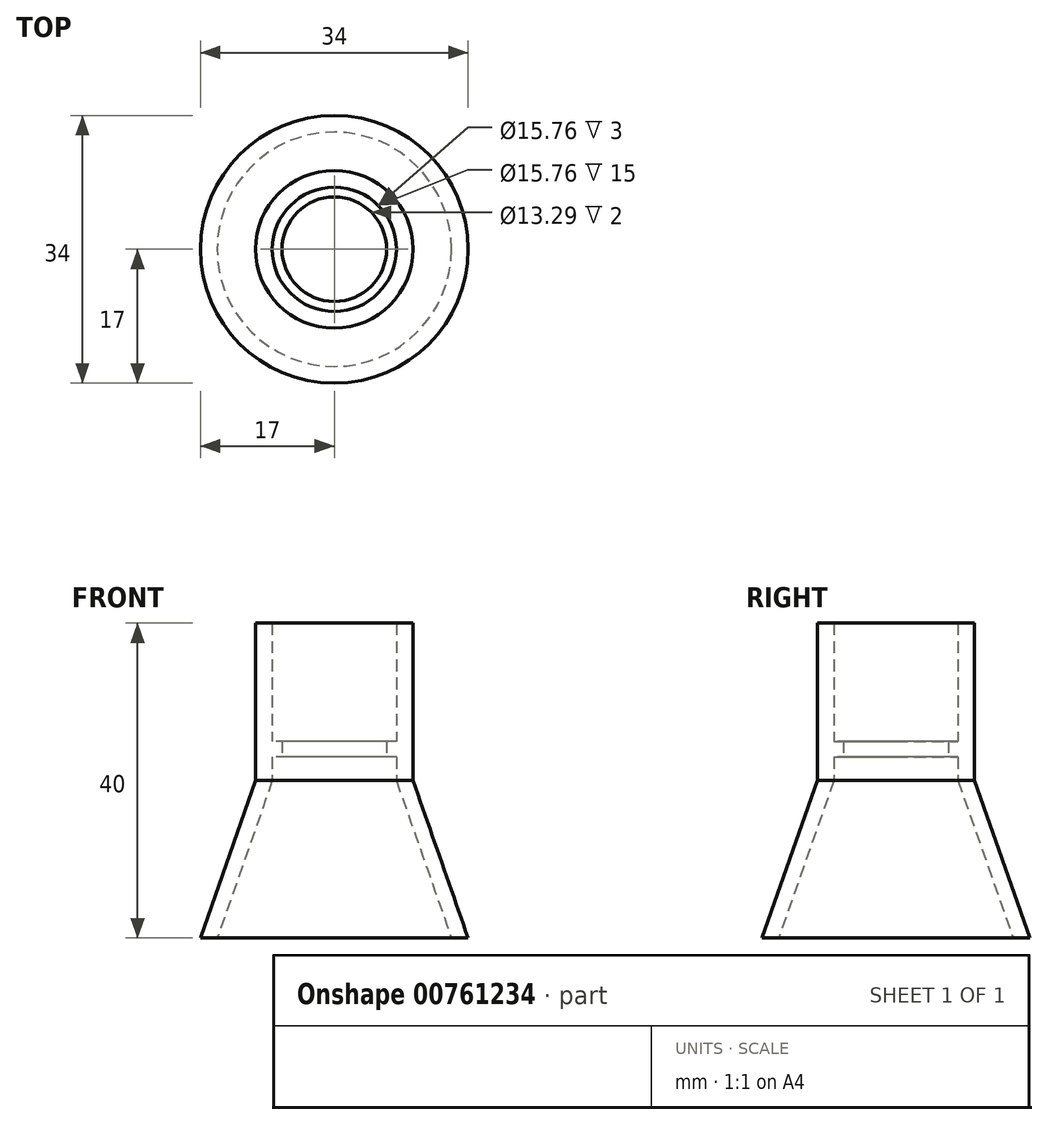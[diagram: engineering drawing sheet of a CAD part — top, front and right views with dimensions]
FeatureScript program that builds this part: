
annotation { "Feature Type Name" : "Feature", "Feature Type Description" : "" }
export const myFeature = defineFeature(function(context is Context, id is Id, definition is map)
    precondition{}
    {
        {
            var Q0;
            Q0=qCreatedBy(makeId("Top.planeOp"),FACE);
            cPlane(context, id + "F0", {"entities" : qUnion([Q0]), "cplaneType" : CPlaneType.OFFSET, "offset" : 20 * mm, "width" : 152.4 * mm, "height" : 152.4 * mm});
        }
        {
            var Q0;
            Q0=qCreatedBy(makeId("Top.planeOp"),FACE);
            var sketch = newSketch(context, id + "F1", { "sketchPlane" : qUnion([Q0])});
            skCircle(sketch, "E0", {"center": v(0, 0) * mm, "radius": 17 * mm});
            skSolve(sketch);
        }
        {
            var Q0;
            Q0=qCreatedBy(id+"F0.planeOp",FACE);
            var sketch = newSketch(context, id + "F2", { "sketchPlane" : qUnion([Q0])});
            skCircle(sketch, "E1", {"center": v(0, 0) * mm, "radius": 10 * mm});
            skSolve(sketch);
        }
        {
            var Q0;
            Q0=qSketchRegion(id+"F1",true);
            var Q1;
            Q1=qSketchRegion(id+"F2",true);
            loft(context, id + "F3", {"sheetProfilesArray" : [{ "sheetProfileEntities" : qUnion([Q0]) }, { "sheetProfileEntities" : qUnion([Q1]) }]});
        }
        {
            var Q0;
            Q0=makeQuery(id+"F3.opLoft","CAP_FACE",FACE,{"disambiguationData":[OSD([makeQuery(id+"F2.imprint","IMPRINT",FACE,{"disambiguationData":[TD([[makeQuery(id+"F2.imprint","IMPRINT",EDGE,{"derivedFrom":sQuery(id+"F2.wireOp",EDGE,"E1")}),1.0]])]})])],"isStart":true});
            var Q1;
            Q1=makeQuery(id+"F3.opLoft","CAP_FACE",FACE,{"disambiguationData":[OSD([makeQuery(id+"F1.imprint","IMPRINT",FACE,{"disambiguationData":[TD([[makeQuery(id+"F1.imprint","IMPRINT",EDGE,{"derivedFrom":sQuery(id+"F1.wireOp",EDGE,"E0")}),1.0]])]})])],"isStart":true});
            shell(context, id + "F4", {"entities" : qUnion([Q0, Q1]), "thickness" : 2 * mm});
        }
        {
            var Q0;
            Q0=qCreatedBy(makeId("Top.planeOp"),FACE);
            cPlane(context, id + "F5", {"entities" : qUnion([Q0]), "cplaneType" : CPlaneType.OFFSET, "offset" : 23 * mm, "width" : 150 * mm, "height" : 150 * mm});
        }
        {
            var Q0;
            Q0=qCreatedBy(id+"F5.planeOp",FACE);
            var sketch = newSketch(context, id + "F6", { "sketchPlane" : qUnion([Q0])});
            skCircle(sketch, "E2", {"center": v(0, 0) * mm, "radius": 6.64 * mm});
            skCircle(sketch, "E3", {"center": v(0, 0) * mm, "radius": 9.64 * mm});
            skSolve(sketch);
        }
        {
            var Q0;
            Q0 = qSketchRegion(id + "F6", true);
            extrude(context, id + "F7", {"entities" : qUnion([Q0]), "operationType" : NewBodyOperationType.ADD, "depth" : 2 * mm, "offsetDistance" : 25 * mm});
        }
        {
            var Q0;
            Q0=makeQuery(id+"F3.opLoft","CAP_FACE",FACE,{"disambiguationData":[OSD([makeQuery(id+"F2.imprint","IMPRINT",FACE,{"disambiguationData":[TD([[makeQuery(id+"F2.imprint","IMPRINT",EDGE,{"derivedFrom":sQuery(id+"F2.wireOp",EDGE,"E1")}),1.0]])]})])],"isStart":true});
            extrude(context, id + "F8", {"entities" : qUnion([Q0]), "operationType" : NewBodyOperationType.ADD, "depth" : 20 * mm, "offsetDistance" : 25 * mm});
        }
    });
